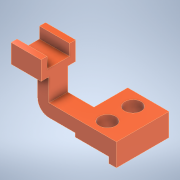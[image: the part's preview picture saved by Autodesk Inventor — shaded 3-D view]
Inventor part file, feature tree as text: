
AUTODESK INVENTOR PART (.ipt)
format: ipt  version: 2021 (Build 250183000, 183)  size: 163,328 bytes
history: native  units: in
note: dims shown in document units (in); Inventor stores cm internally (conversion verified against a paired STEP export)
features: extrude x4, sketch x4, fillet x1
ambient origin geometry x8: Origin, YZ Plane, XZ Plane, XY Plane, X Axis, Y Axis, Z Axis, Center Point
bodies: Solid1 (feature_tree)
feature tree (9):
  extrude  "Extrusion1"  Depth=3.1496in
  extrude  "Extrusion2"  Depth=1.9685in
  extrude  "Extrusion3"  Depth=18.5039in
  fillet  "Fillet1"  Radius=5.9055in
  extrude  "Extrusion4"  Depth=27.5591in TaperAngle=0.0deg
  sketch  "Sketch1"  dims[d0=3.937in d1=3.1496in]
  sketch  "Sketch2"  dims[d2=17.7165in d3=1.9685in]
  sketch  "Sketch3"  dims[d4=19.685in d5=18.5039in d6=5.9055in]
  sketch  "Sketch4"  dims[d7=11.811in d8=27.5591in d9=0.0in d10=1.9685in d11=19.685in d12=18.5039in d13=5.9055in d14=11.811in d15=9.8425in d16=0.0in d17=4.1339in d18=9.8425in d19=3.1496in d20=5.9055in d21=11.811in d22=3.1496in d23=15.748in d24=0.0in d25=5.9055in d26=7.0866in d27=11.811in d28=13.3858in d29=8.6614in d30=8.6614in d31=17.6855in d32=0.0in d33=0.1969in d34=0.0344in]
